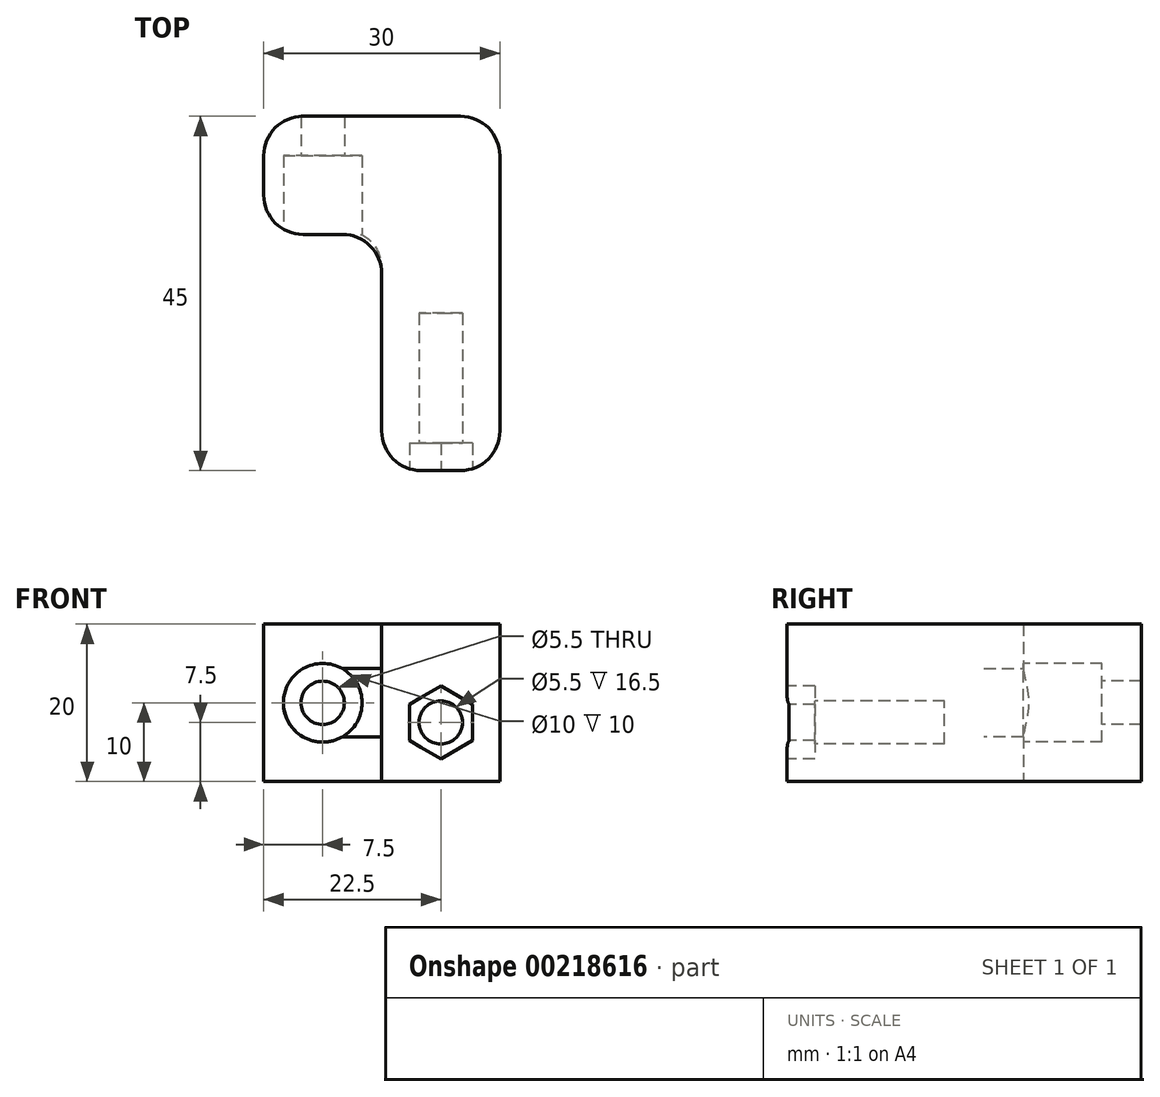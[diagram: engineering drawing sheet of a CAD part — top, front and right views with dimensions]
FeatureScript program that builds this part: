
annotation { "Feature Type Name" : "Feature", "Feature Type Description" : "" }
export const myFeature = defineFeature(function(context is Context, id is Id, definition is map)
    precondition{}
    {
        {
            var Q0;
            Q0=qCreatedBy(makeId("Top.planeOp"),FACE);
            var sketch = newSketch(context, id + "F0", { "sketchPlane" : qUnion([Q0])});
            skLineSegment(sketch, "E0", {"start": v(0, 0) * mm, "end": v(0, 45) * mm});
            skLineSegment(sketch, "E1", {"start": v(0, 45) * mm, "end": v(-30, 45) * mm});
            skLineSegment(sketch, "E2", {"start": v(-30, 45) * mm, "end": v(-30, 30) * mm});
            skLineSegment(sketch, "E3", {"start": v(-30, 30) * mm, "end": v(-15, 30) * mm});
            skLineSegment(sketch, "E4", {"start": v(-15, 30) * mm, "end": v(-15, 0) * mm});
            skLineSegment(sketch, "E5", {"start": v(-15, 0) * mm, "end": v(0, 0) * mm});
            skSolve(sketch);
        }
        {
            var Q0;
            Q0 = qSketchRegion(id + "F0", true);
            extrude(context, id + "F1", {"entities" : qUnion([Q0]), "depth" : 20 * mm, "offsetDistance" : 25 * mm});
        }
        {
            var Q0;
            Q0=makeQuery(id+"F1.opExtrude","SWEPT_FACE",FACE,{"disambiguationData":[OSD([sQuery(id+"F0.wireOp",EDGE,"E5")])]});
            var sketch = newSketch(context, id + "F2", { "sketchPlane" : qUnion([Q0])});
            skCircle(sketch, "E6", {"center": v(-7.5, 7.5) * mm, "radius": 2.75 * mm});
            skSolve(sketch);
        }
        {
            var Q0;
            Q0 = qSketchRegion(id + "F2", true);
            extrude(context, id + "F3", {"entities" : qUnion([Q0]), "operationType" : NewBodyOperationType.REMOVE, "oppositeDirection" : true, "depth" : 20 * mm, "offsetDistance" : 25 * mm});
        }
        {
            var Q0;
            Q0=makeQuery(id+"F1.opExtrude","SWEPT_FACE",FACE,{"disambiguationData":[OSD([sQuery(id+"F0.wireOp",EDGE,"E5")])]});
            var sketch = newSketch(context, id + "F4", { "sketchPlane" : qUnion([Q0])});
            skCircle(sketch, "E7.cCircle", {"center": v(-7.5, 7.5) * mm, "radius": 4 * mm, "construction": true});
            skLineSegment(sketch, "E7.0", {"start": v(-3.5, 5.2) * mm, "end": v(-7.5, 2.88) * mm});
            skLineSegment(sketch, "E7.1", {"start": v(-7.5, 2.88) * mm, "end": v(-11.5, 5.2) * mm});
            skLineSegment(sketch, "E7.2", {"start": v(-11.5, 5.2) * mm, "end": v(-11.5, 9.8) * mm});
            skLineSegment(sketch, "E7.3", {"start": v(-11.5, 9.8) * mm, "end": v(-7.5, 12.12) * mm});
            skLineSegment(sketch, "E7.4", {"start": v(-7.5, 12.12) * mm, "end": v(-3.5, 9.8) * mm});
            skLineSegment(sketch, "E7.5", {"start": v(-3.5, 9.8) * mm, "end": v(-3.5, 5.2) * mm});
            skPoint(sketch, "E7.0.midPoint", {"position": v(-5.5, 4.04) * mm});
            skSolve(sketch);
        }
        {
            var Q0;
            Q0 = qSketchRegion(id + "F4", true);
            extrude(context, id + "F5", {"entities" : qUnion([Q0]), "operationType" : NewBodyOperationType.REMOVE, "oppositeDirection" : true, "depth" : 3.5 * mm, "offsetDistance" : 25 * mm});
        }
        {
            var Q0;
            Q0=makeQuery(id+"F1.opExtrude","SWEPT_FACE",FACE,{"disambiguationData":[OSD([sQuery(id+"F0.wireOp",EDGE,"E3")])]});
            var sketch = newSketch(context, id + "F6", { "sketchPlane" : qUnion([Q0])});
            skCircle(sketch, "E8", {"center": v(-22.5, 10) * mm, "radius": 2.75 * mm});
            skSolve(sketch);
        }
        {
            var Q0;
            Q0 = qSketchRegion(id + "F6", true);
            extrude(context, id + "F7", {"entities" : qUnion([Q0]), "operationType" : NewBodyOperationType.REMOVE, "endBound" : BoundingType.THROUGH_ALL, "oppositeDirection" : true, "depth" : 25 * mm, "offsetDistance" : 25 * mm});
        }
        {
            var Q0;
            Q0=makeQuery(id+"F1.opExtrude","SWEPT_FACE",FACE,{"disambiguationData":[OSD([sQuery(id+"F0.wireOp",EDGE,"E3")])]});
            var sketch = newSketch(context, id + "F8", { "sketchPlane" : qUnion([Q0])});
            skCircle(sketch, "E9", {"center": v(-22.5, 10) * mm, "radius": 5 * mm});
            skSolve(sketch);
        }
        {
            var Q0;
            Q0 = qSketchRegion(id + "F8", true);
            extrude(context, id + "F9", {"entities" : qUnion([Q0]), "operationType" : NewBodyOperationType.REMOVE, "oppositeDirection" : true, "depth" : 10 * mm, "offsetDistance" : 25 * mm});
        }
        {
            var Q0;
            Q0=makeQuery(id+"F1.opExtrude","SWEPT_EDGE",EDGE,{"disambiguationData":[OSD([sQuery(id+"F0.wireOp",EDGE,"E3"),sQuery(id+"F0.wireOp",EDGE,"E4")])]});
            var Q1;
            Q1=makeQuery(id+"F1.opExtrude","SWEPT_EDGE",EDGE,{"disambiguationData":[OSD([sQuery(id+"F0.wireOp",EDGE,"E2"),sQuery(id+"F0.wireOp",EDGE,"E3")])]});
            var Q2;
            Q2=makeQuery(id+"F1.opExtrude","SWEPT_EDGE",EDGE,{"disambiguationData":[OSD([sQuery(id+"F0.wireOp",EDGE,"E1"),sQuery(id+"F0.wireOp",EDGE,"E2")])]});
            var Q3;
            Q3=makeQuery(id+"F1.opExtrude","SWEPT_EDGE",EDGE,{"disambiguationData":[OSD([sQuery(id+"F0.wireOp",EDGE,"E4"),sQuery(id+"F0.wireOp",EDGE,"E5")])]});
            var Q4;
            Q4=makeQuery(id+"F1.opExtrude","SWEPT_EDGE",EDGE,{"disambiguationData":[OSD([sQuery(id+"F0.wireOp",EDGE,"E0"),sQuery(id+"F0.wireOp",EDGE,"E5")])]});
            var Q5;
            Q5=makeQuery(id+"F1.opExtrude","SWEPT_EDGE",EDGE,{"disambiguationData":[OSD([sQuery(id+"F0.wireOp",EDGE,"E0"),sQuery(id+"F0.wireOp",EDGE,"E1")])]});
            fillet(context, id + "F10", {"entities" : qUnion([Q0, Q1, Q2, Q3, Q4, Q5]), "tangentPropagation" : true, "radius" : 5 * mm, "defaultsChanged" : false, "vertexSettings" : [], "allowEdgeOverflow" : false});
        }
    });
